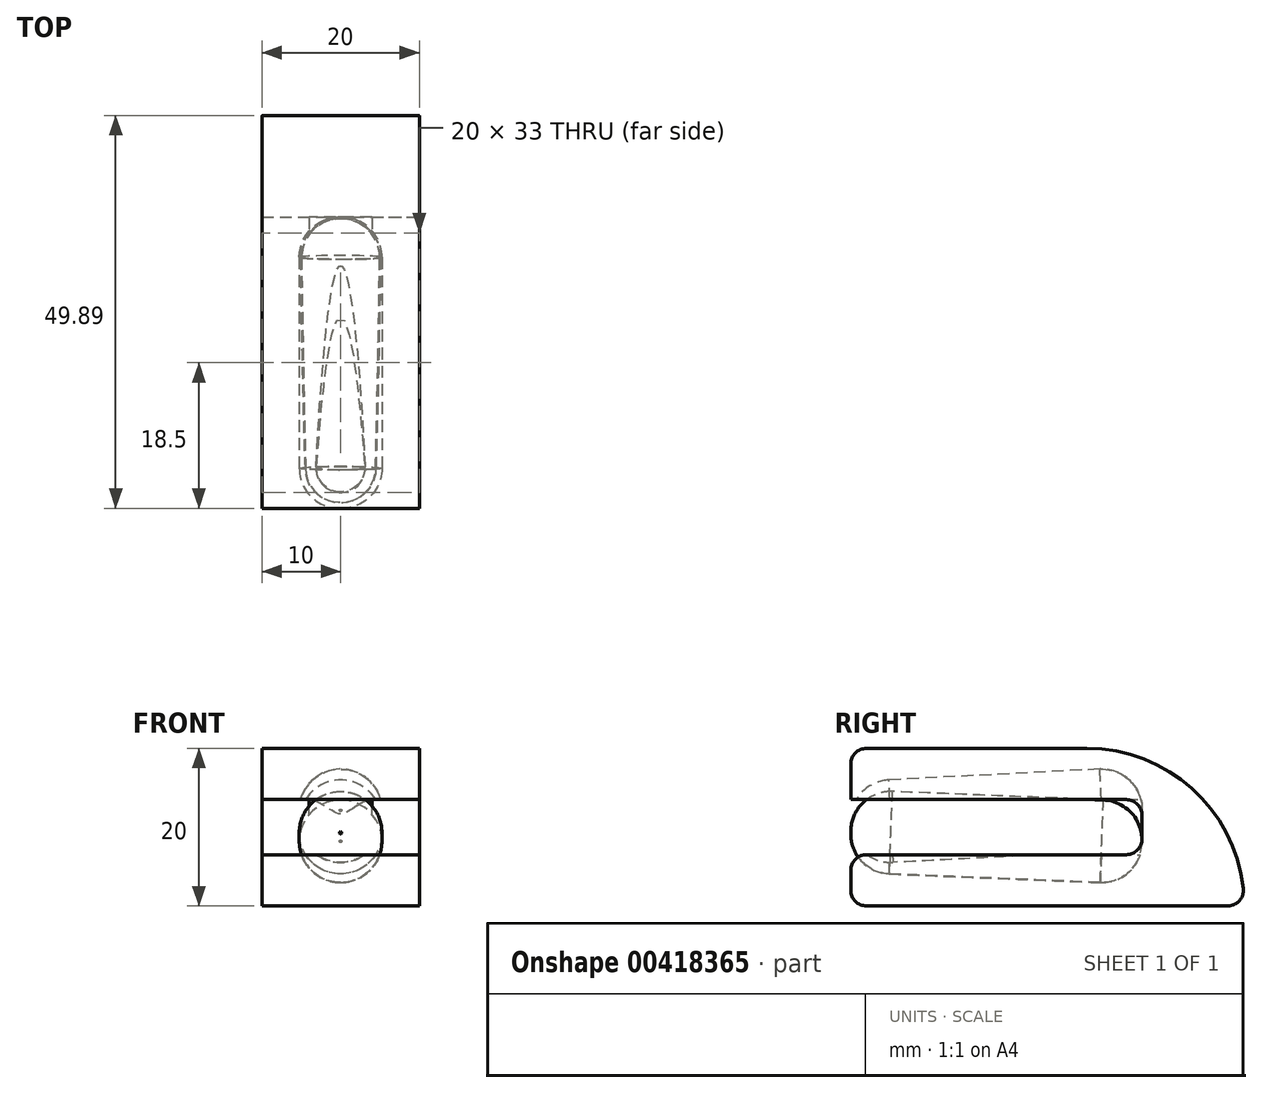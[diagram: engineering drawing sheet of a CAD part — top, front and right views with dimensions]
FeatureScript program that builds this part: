
annotation { "Feature Type Name" : "Feature", "Feature Type Description" : "" }
export const myFeature = defineFeature(function(context is Context, id is Id, definition is map)
    precondition{}
    {
        {
            var Q0;
            Q0=qCreatedBy(makeId("Top.planeOp"),FACE);
            var sketch = newSketch(context, id + "F0", { "sketchPlane" : qUnion([Q0])});
            skLineSegment(sketch, "E0.bottom", {"start": v(-10, 25) * mm, "end": v(10, 25) * mm});
            skLineSegment(sketch, "E0.top", {"start": v(-10, -25) * mm, "end": v(10, -25) * mm});
            skLineSegment(sketch, "E0.left", {"start": v(-10, 25) * mm, "end": v(-10, -25) * mm});
            skLineSegment(sketch, "E0.right", {"start": v(10, 25) * mm, "end": v(10, -25) * mm});
            skPoint(sketch, "E0.middle", {"position": v(0, 0) * mm});
            skSolve(sketch);
        }
        {
            var Q0;
            Q0 = qSketchRegion(id + "F0", true);
            extrude(context, id + "F1", {"entities" : qUnion([Q0]), "depth" : 20 * mm});
        }
        {
            var Q0;
            Q0=makeQuery(id+"F1.opExtrude","CAP_EDGE",EDGE,{"disambiguationData":[OSD([sQuery(id+"F0.wireOp",EDGE,"E0.bottom")])],"isStart":false});
            fillet(context, id + "F2", {"entities" : qUnion([Q0]), "radius" : 20 * mm, "tangentPropagation" : true, "allowEdgeOverflow" : false});
        }
        {
            var Q0;
            Q0=makeQuery(id+"F1.opExtrude","SWEPT_FACE",FACE,{"disambiguationData":[OSD([sQuery(id+"F0.wireOp",EDGE,"E0.top")])]});
            var sketch = newSketch(context, id + "F3", { "sketchPlane" : qUnion([Q0])});
            skLineSegment(sketch, "E1", {"start": v(0, 0) * mm, "end": v(0, 20) * mm, "construction": true});
            skLineSegment(sketch, "E2.bottom", {"start": v(-10, 13.5) * mm, "end": v(10, 13.5) * mm});
            skLineSegment(sketch, "E2.top", {"start": v(-10, 6.5) * mm, "end": v(10, 6.5) * mm});
            skLineSegment(sketch, "E2.left", {"start": v(-10, 13.5) * mm, "end": v(-10, 6.5) * mm});
            skLineSegment(sketch, "E2.right", {"start": v(10, 13.5) * mm, "end": v(10, 6.5) * mm});
            skPoint(sketch, "E2.middle", {"position": v(0, 10) * mm});
            skSolve(sketch);
        }
        {
            var Q0;
            Q0 = qSketchRegion(id + "F3", true);
            extrude(context, id + "F4", {"entities" : qUnion([Q0]), "operationType" : NewBodyOperationType.REMOVE, "oppositeDirection" : true, "depth" : 37 * mm});
        }
        {
            var Q0;
            {var subQ2=sQuery(id+"F0.wireOp",EDGE,"E0.top");Q0=makeQuery(id+"F4.boolean.opBoolean","SPLIT",FACE,{"disambiguationData":[TD([makeQuery(id+"F4.opExtrude","SWEPT_FACE",FACE,{"disambiguationData":[OSD([sQuery(id+"F3.wireOp",EDGE,"E2.bottom")])]})])],"derivedFrom":makeQuery(id+"F1.opExtrude","SWEPT_FACE",FACE,{"disambiguationData":[OSD([subQ2])]})});}
            var Q1;
            Q1 = qBodyType(qCreatedBy(id + "F6" ,EDGE), BodyType.WIRE);
            cPlane(context, id + "F5", {"entities" : qUnion([Q0, Q1]), "cplaneType" : CPlaneType.OFFSET, "offset" : 0 * mm, "width" : 150 * mm, "height" : 150 * mm});
        }
        {
            var Q0;
            Q0=qCreatedBy(id+"F5.planeOp",FACE);
            var sketch = newSketch(context, id + "F6", { "sketchPlane" : qUnion([Q0])});
            skPoint(sketch, "E3.0", {"position": v(0, 20) * mm});
            skLineSegment(sketch, "E4", {"start": v(0, 0) * mm, "end": v(0, 20) * mm, "construction": true});
            skPoint(sketch, "E5", {"position": v(0, 9.5) * mm});
            skPoint(sketch, "E6", {"position": v(0, 10) * mm});
            skCircle(sketch, "E7", {"center": v(0, 9.5) * mm, "radius": 5.25 * mm});
            skSolve(sketch);
        }
        {
            var Q0;
            Q0=qCreatedBy(id+"F5.planeOp",FACE);
            var sketch = newSketch(context, id + "F7", { "sketchPlane" : qUnion([Q0])});
            skPoint(sketch, "E8.0", {"position": v(0, 10) * mm});
            skLineSegment(sketch, "E8.1", {"start": v(0, 0) * mm, "end": v(0, 20) * mm, "construction": true});
            skPoint(sketch, "E9", {"position": v(0, 10.5) * mm});
            skCircle(sketch, "E10", {"center": v(0, 10.5) * mm, "radius": 5.25 * mm});
            skSolve(sketch);
        }
        {
            var Q0;
            Q0=makeQuery(id+"F4.boolean.opBoolean","COPY",FACE,{"derivedFrom":makeQuery(id+"F4.opExtrude","CAP_FACE",FACE,{"disambiguationData":[OSD([sQuery(id+"F3.wireOp",EDGE,"E2.bottom"),sQuery(id+"F3.wireOp",EDGE,"E2.top"),sQuery(id+"F3.wireOp",EDGE,"E2.left"),sQuery(id+"F3.wireOp",EDGE,"E2.right")])],"isStart":false})});
            cPlane(context, id + "F8", {"entities" : qUnion([Q0]), "cplaneType" : CPlaneType.OFFSET, "offset" : 0 * mm, "width" : 150 * mm, "height" : 150 * mm});
        }
        {
            var Q0;
            Q0=qCreatedBy(id+"F8.planeOp",FACE);
            var sketch = newSketch(context, id + "F9", { "sketchPlane" : qUnion([Q0])});
            skLineSegment(sketch, "E11", {"start": v(0, 8) * mm, "end": v(0, 12) * mm, "construction": true});
            skPoint(sketch, "E12.0", {"position": v(0, 10) * mm});
            skPoint(sketch, "E13", {"position": v(0, 12) * mm});
            skPoint(sketch, "E14", {"position": v(0, 8) * mm});
            skCircle(sketch, "E15", {"center": v(0, 8) * mm, "radius": 5.25 * mm});
            skSolve(sketch);
        }
        {
            var Q0;
            Q0=qCreatedBy(id+"F8.planeOp",FACE);
            var sketch = newSketch(context, id + "F10", { "sketchPlane" : qUnion([Q0])});
            skLineSegment(sketch, "E16", {"start": v(0, 8.4) * mm, "end": v(0, 12.4) * mm, "construction": true});
            skPoint(sketch, "E17.0", {"position": v(0, 10.4) * mm});
            skPoint(sketch, "E18", {"position": v(0, 12.4) * mm});
            skPoint(sketch, "E19", {"position": v(0, 8.4) * mm});
            skCircle(sketch, "E20", {"center": v(0, 12.4) * mm, "radius": 5.25 * mm});
            skSolve(sketch);
        }
        {
            var Q0;
            Q0=makeQuery(id+"F1.opExtrude","CAP_EDGE",EDGE,{"disambiguationData":[OSD([sQuery(id+"F0.wireOp",EDGE,"E0.top")])],"isStart":false});
            var Q1;
            Q1=makeQuery(id+"F4.boolean.opBoolean","COPY",EDGE,{"derivedFrom":makeQuery(id+"F4.opExtrude","CAP_EDGE",EDGE,{"disambiguationData":[OSD([sQuery(id+"F3.wireOp",EDGE,"E2.bottom")])],"isStart":true})});
            var Q2;
            Q2=makeQuery(id+"F4.boolean.opBoolean","COPY",EDGE,{"derivedFrom":makeQuery(id+"F4.opExtrude","CAP_EDGE",EDGE,{"disambiguationData":[OSD([sQuery(id+"F3.wireOp",EDGE,"E2.top")])],"isStart":true})});
            var Q3;
            Q3=makeQuery(id+"F1.opExtrude","CAP_EDGE",EDGE,{"disambiguationData":[OSD([sQuery(id+"F0.wireOp",EDGE,"E0.top")])],"isStart":true});
            var Q4;
            Q4=makeQuery(id+"F4.boolean.opBoolean","COPY",EDGE,{"derivedFrom":makeQuery(id+"F4.opExtrude","CAP_EDGE",EDGE,{"disambiguationData":[OSD([sQuery(id+"F3.wireOp",EDGE,"E2.top")])],"isStart":false})});
            var Q5;
            Q5=makeQuery(id+"F4.boolean.opBoolean","COPY",EDGE,{"derivedFrom":makeQuery(id+"F4.opExtrude","CAP_EDGE",EDGE,{"disambiguationData":[OSD([sQuery(id+"F3.wireOp",EDGE,"E2.bottom")])],"isStart":false})});
            var Q6;
            {var subQ0=sQuery(id+"F0.wireOp",EDGE,"E0.bottom");Q6=makeQuery(id+"F2.opFillet","BLEND_EDGE",EDGE,{"blendedFrom":[makeQuery(id+"F1.opExtrude","CAP_EDGE",EDGE,{"disambiguationData":[OSD([subQ0])],"isStart":false}),makeQuery(id+"F1.opExtrude","CAP_FACE",FACE,{"disambiguationData":[OSD([subQ0,sQuery(id+"F0.wireOp",EDGE,"E0.top"),sQuery(id+"F0.wireOp",EDGE,"E0.left"),sQuery(id+"F0.wireOp",EDGE,"E0.right")])],"isStart":true})],"blendedInto":[makeQuery(id+"F1.opExtrude","CAP_FACE",FACE,{"disambiguationData":[OSD([subQ0,sQuery(id+"F0.wireOp",EDGE,"E0.top"),sQuery(id+"F0.wireOp",EDGE,"E0.left"),sQuery(id+"F0.wireOp",EDGE,"E0.right")])],"isStart":true})]});}
            fillet(context, id + "F11", {"entities" : qUnion([Q0, Q1, Q2, Q3, Q4, Q5, Q6]), "radius" : 2 * mm, "tangentPropagation" : true, "allowEdgeOverflow" : false});
        }
        {
            var Q1;
            Q1=makeQuery(id+"F10.imprint","IMPRINT",FACE,{"disambiguationData":[TD([[makeQuery(id+"F10.imprint","IMPRINT",EDGE,{"derivedFrom":sQuery(id+"F10.wireOp",EDGE,"E20")}),1.0]])]});
            var Q2;
            Q2=makeQuery(id+"F7.imprint","IMPRINT",FACE,{"disambiguationData":[TD([[makeQuery(id+"F7.imprint","IMPRINT",EDGE,{"derivedFrom":sQuery(id+"F7.wireOp",EDGE,"E10")}),1.0]])]});
            loft(context, id + "F12", {"sheetProfilesArray" : [{ "sheetProfileEntities" : qUnion([Q1]) }, { "sheetProfileEntities" : qUnion([Q2]) }]});
        }
        {
            var Q0;
            Q0=makeQuery(id+"F9.imprint","IMPRINT",FACE,{"disambiguationData":[TD([[makeQuery(id+"F9.imprint","IMPRINT",EDGE,{"derivedFrom":sQuery(id+"F9.wireOp",EDGE,"E15")}),1.0]])]});
            var Q1;
            Q1=makeQuery(id+"F6.imprint","IMPRINT",FACE,{"disambiguationData":[TD([[makeQuery(id+"F6.imprint","IMPRINT",EDGE,{"derivedFrom":sQuery(id+"F6.wireOp",EDGE,"E7")}),1.0]])]});
            loft(context, id + "F13", {"sheetProfilesArray" : [{ "sheetProfileEntities" : qUnion([Q0]) }, { "sheetProfileEntities" : qUnion([Q1]) }]});
        }
        {
            var Q0;
            Q0=makeQuery(id+"F12.opLoft","CAP_FACE",FACE,{"disambiguationData":[OSD([makeQuery(id+"F7.imprint","IMPRINT",FACE,{"disambiguationData":[TD([[makeQuery(id+"F7.imprint","IMPRINT",EDGE,{"derivedFrom":sQuery(id+"F7.wireOp",EDGE,"E10")}),1.0]])]})])],"isStart":true});
            var Q1;
            Q1=makeQuery(id+"F13.opLoft","CAP_FACE",FACE,{"disambiguationData":[OSD([makeQuery(id+"F6.imprint","IMPRINT",FACE,{"disambiguationData":[TD([[makeQuery(id+"F6.imprint","IMPRINT",EDGE,{"derivedFrom":sQuery(id+"F6.wireOp",EDGE,"E7")}),1.0]])]})])],"isStart":true});
            var Q2;
            Q2=makeQuery(id+"F12.opLoft","CAP_FACE",FACE,{"disambiguationData":[OSD([makeQuery(id+"F10.imprint","IMPRINT",FACE,{"disambiguationData":[TD([[makeQuery(id+"F10.imprint","IMPRINT",EDGE,{"derivedFrom":sQuery(id+"F10.wireOp",EDGE,"E20")}),1.0]])]})])],"isStart":true});
            var Q3;
            Q3=makeQuery(id+"F13.opLoft","CAP_FACE",FACE,{"disambiguationData":[OSD([makeQuery(id+"F9.imprint","IMPRINT",FACE,{"disambiguationData":[TD([[makeQuery(id+"F9.imprint","IMPRINT",EDGE,{"derivedFrom":sQuery(id+"F9.wireOp",EDGE,"E15")}),1.0]])]})])],"isStart":true});
            fillet(context, id + "F14", {"entities" : qUnion([Q0, Q1, Q2, Q3]), "radius" : 5.1 * mm, "tangentPropagation" : true, "allowEdgeOverflow" : false});
        }
        {
            var Q0;
            Q0=makeQuery(id+"F12.opLoft","SWEPT_BODY",BODY,{"disambiguationData":[OSD([makeQuery(id+"F6.imprint","IMPRINT",FACE,{"disambiguationData":[TD([[makeQuery(id+"F6.imprint","IMPRINT",EDGE,{"derivedFrom":sQuery(id+"F6.wireOp",EDGE,"gOrBsAt7-1QjJ-F9uG-XKRJ-JXm2eGmSJvml")}),1.0]])]}),makeQuery(id+"F10.imprint","IMPRINT",FACE,{"disambiguationData":[TD([[makeQuery(id+"F10.imprint","IMPRINT",EDGE,{"derivedFrom":sQuery(id+"F10.wireOp",EDGE,"E20")}),1.0]])]})])]});
            var Q1;
            Q1=makeQuery(id+"F1.opExtrude","SWEPT_BODY",BODY,{"disambiguationData":[OSD([sQuery(id+"F0.wireOp",EDGE,"E0.bottom"),sQuery(id+"F0.wireOp",EDGE,"E0.top"),sQuery(id+"F0.wireOp",EDGE,"E0.left"),sQuery(id+"F0.wireOp",EDGE,"E0.right")])]});
            booleanBodies(context, id + "F15", {"operationType" : BooleanOperationType.SUBTRACTION, "tools" : qUnion([Q0]), "targets" : qUnion([Q1])});
        }
    });
